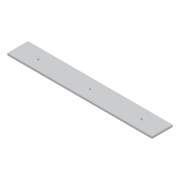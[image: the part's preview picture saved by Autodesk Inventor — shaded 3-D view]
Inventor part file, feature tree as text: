
AUTODESK INVENTOR PART (.ipt)
format: ipt  version: 2016 (Build 200138000, 138)  size: 81,408 bytes
history: native  units: mm
features: sketch x2, extrude x1, hole x1
ambient origin geometry x8: Origin, YZ Plane, XZ Plane, XY Plane, X Axis, Y Axis, Z Axis, Center Point
bodies: Volumenkörper1 (feature_tree)
feature tree (4):
  extrude  "Extrusion1"  Depth=700.0mm
  hole  "Bohrung1"  [1 undecoded]
  sketch  "Skizze1"  dims[d2=10.0mm d3=0.0mm d4=700.0mm]
  sketch  "Skizze2"  dims[d5=100.0mm d6=500.0mm d7=6.6mm d8=6.0mm d9=14.5mm d10=6.6mm d11=90.0deg d12=8.0mm d13=20.594885mm]
note: 1 required parameter value undecoded (feature->parameter linkage not recoverable at this tier; creation-order binding heuristic only, values carry confidence <= 0.55)
